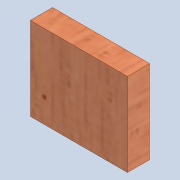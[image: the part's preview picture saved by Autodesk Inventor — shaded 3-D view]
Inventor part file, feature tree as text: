
AUTODESK INVENTOR PART (.ipt)
format: ipt  version: 2020 (Build 240168000, 168)  size: 238,080 bytes
history: native  units: mm
features: other x3, sketch x2, reference x2, extrude x1, hole x1
ambient origin geometry x8: Origin, YZ Plane, XZ Plane, XY Plane, X Axis, Y Axis, Z Axis, Center Point
bodies: Solid1 (feature_tree)
feature tree (9):
  extrude  "Extrusion1"  Depth=30.0mm
  hole  "Hole1"  [1 undecoded]
  sketch  "Sketch1"  dims[d0=35.0mm d1=30.0mm]
  sketch  "Sketch6"  dims[d2=8.0mm d3=0.0mm d37=2.459mm d38=8.0mm d39=4.0mm d40=2.0mm d41=90.0deg d42=8.8mm d43=20.594885mm]
  reference  "Reference1"
  reference  "Reference2"
  parser-record x1  (decoder bookkeeping rows leaked as tree rows — omitted from the tree; the rows remain in map.json)
  other  "0005-00-00 Ansamblu_General_V1.iam"
  other  "0005-20-1003 Switch:1"
note: 1 required parameter value undecoded (feature->parameter linkage not recoverable at this tier; creation-order binding heuristic only, values carry confidence <= 0.55)
note: 1 file-system path scrubbed to <path> (originals preserved in map.json)
